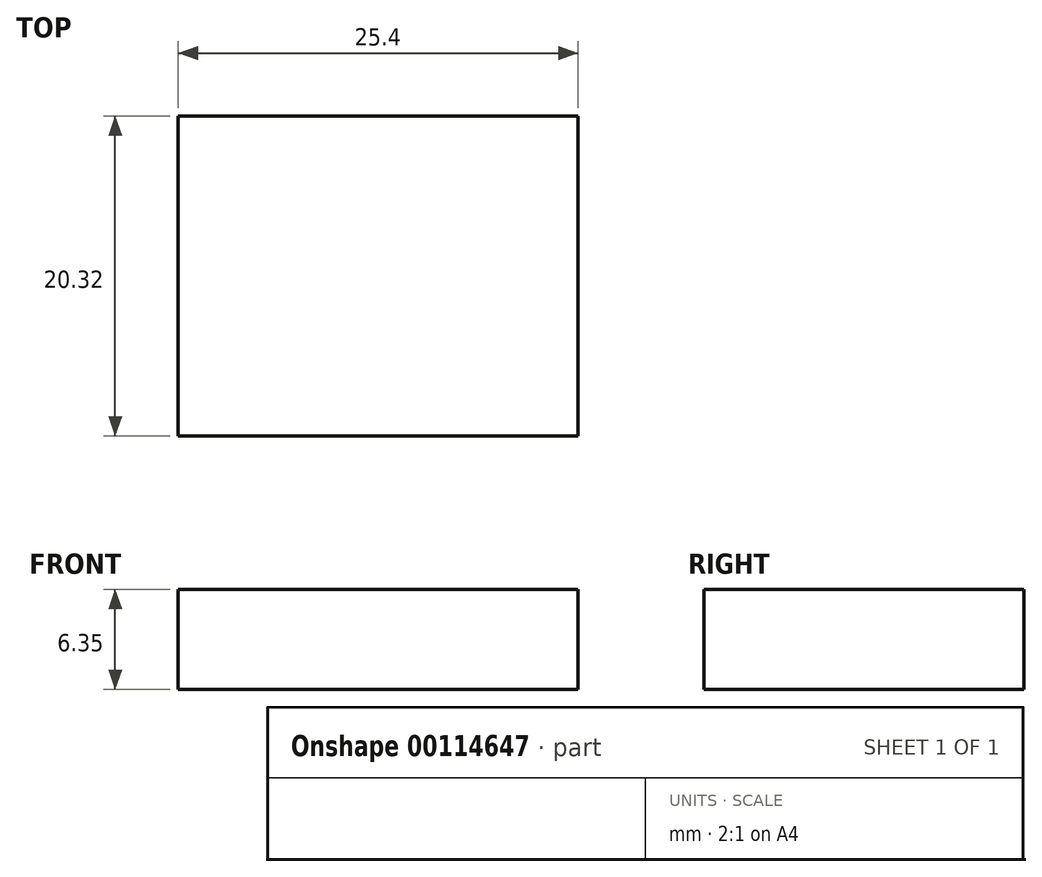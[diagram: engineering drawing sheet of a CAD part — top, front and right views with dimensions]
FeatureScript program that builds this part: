
annotation { "Feature Type Name" : "Feature", "Feature Type Description" : "" }
export const myFeature = defineFeature(function(context is Context, id is Id, definition is map)
    precondition{}
    {
        {
            var Q0;
            Q0=qCreatedBy(makeId("Top.planeOp"),FACE);
            var sketch = newSketch(context, id + "F0", { "sketchPlane" : qUnion([Q0])});
            skLineSegment(sketch, "E0.bottom", {"start": v(0, 0) * mm, "end": v(25.4, 0) * mm});
            skLineSegment(sketch, "E0.top", {"start": v(0, -20.32) * mm, "end": v(25.4, -20.32) * mm});
            skLineSegment(sketch, "E0.left", {"start": v(0, 0) * mm, "end": v(0, -20.32) * mm});
            skLineSegment(sketch, "E0.right", {"start": v(25.4, 0) * mm, "end": v(25.4, -20.32) * mm});
            skSolve(sketch);
        }
        {
            var Q0;
            Q0=makeQuery(id+"F0.imprint","IMPRINT",FACE,{"disambiguationData":[TD([[makeQuery(id+"F0.imprint","IMPRINT",EDGE,{"derivedFrom":sQuery(id+"F0.wireOp",EDGE,"E0.bottom")}),-1.0]])]});
            extrude(context, id + "F1", {"entities" : qUnion([Q0]), "depth" : 6.35 * mm});
        }
    });
